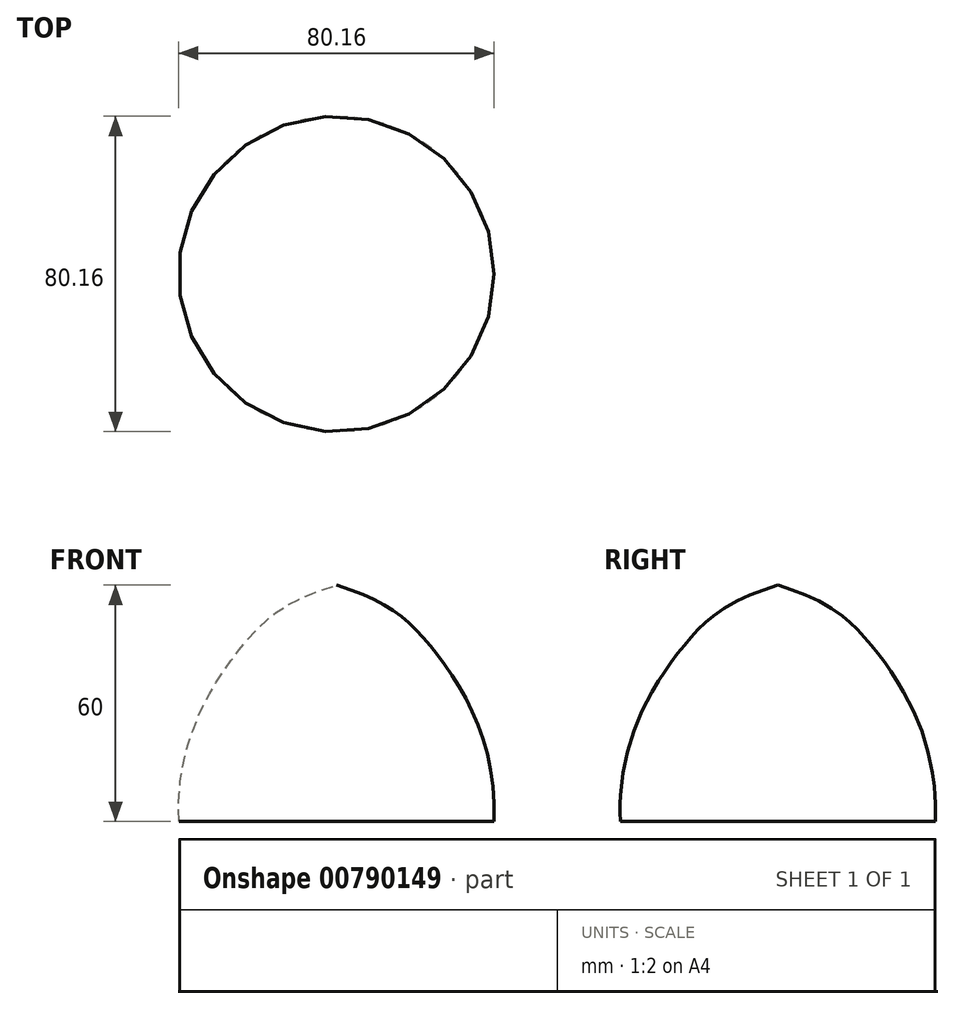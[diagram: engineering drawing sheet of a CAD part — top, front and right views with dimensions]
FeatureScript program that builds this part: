
annotation { "Feature Type Name" : "Feature", "Feature Type Description" : "" }
export const myFeature = defineFeature(function(context is Context, id is Id, definition is map)
    precondition{}
    {
        {
            var Q0;
            Q0=qCreatedBy(makeId("Front.planeOp"),FACE);
            var sketch = newSketch(context, id + "F0", { "sketchPlane" : qUnion([Q0])});
            skLineSegment(sketch, "E0", {"start": v(0, 0) * mm, "end": v(40, 0) * mm});
            skLineSegment(sketch, "E1", {"start": v(0, 0) * mm, "end": v(0, 60) * mm});
            skFitSpline(sketch, "E2", {"points": [v(0, 60) * mm, v(23.96, 44.49) * mm, v(40, 0) * mm], "startDerivative": vector(87.2, -26.56) * mm, "endDerivative": vector(-5.35, -106.52) * mm});
            skSolve(sketch);
        }
        {
            var Q0;
            Q0=makeQuery(id+"F0.imprint","IMPRINT",FACE,{"disambiguationData":[TD([[makeQuery(id+"F0.imprint","IMPRINT",EDGE,{"derivedFrom":sQuery(id+"F0.wireOp",EDGE,"E0")}),1.0]])]});
            var Q1;
            Q1=sQuery(id+"F0.wireOp",EDGE,"E1");
            revolve(context, id + "F1", {"surfaceOperationType" : NewSurfaceOperationType.NEW, "entities" : qUnion([Q0]), "axis" : qUnion([Q1]), "revolveType" : RevolveType.FULL});
        }
        {
            var Q0;
            Q0=makeQuery(id+"F1.opRevolve","SWEPT_BODY",BODY,{"disambiguationData":[OSD([sQuery(id+"F0.wireOp",EDGE,"E0"),sQuery(id+"F0.wireOp",EDGE,"E1"),sQuery(id+"F0.wireOp",EDGE,"E2")])]});
            transform(context, id + "F2", {"entities" : qUnion([Q0]), "transformType" : TransformType.TRANSLATION_3D, "dx" : 0 * mm, "dy" : 0 * mm, "dz" : 0 * mm, "makeCopy" : true});
        }
    });
